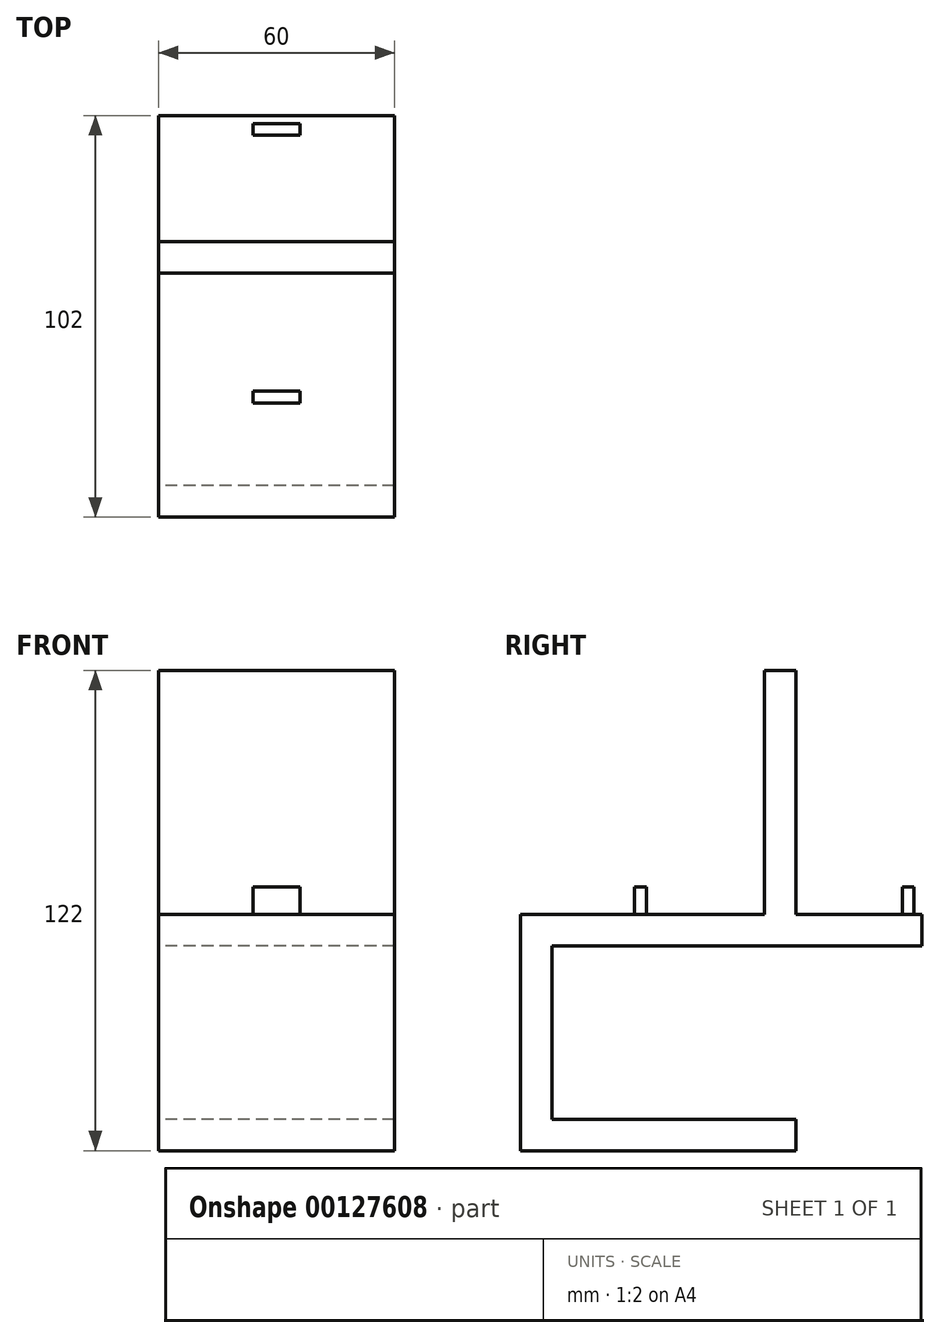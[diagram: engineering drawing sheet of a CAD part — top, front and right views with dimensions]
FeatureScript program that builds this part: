
annotation { "Feature Type Name" : "Feature", "Feature Type Description" : "" }
export const myFeature = defineFeature(function(context is Context, id is Id, definition is map)
    precondition{}
    {
        {
            var Q0;
            Q0=qCreatedBy(makeId("Right.planeOp"),FACE);
            var sketch = newSketch(context, id + "F0", { "sketchPlane" : qUnion([Q0])});
            skLineSegment(sketch, "E0.bottom", {"start": v(129.92, 70) * mm, "end": v(121.92, 70) * mm});
            skLineSegment(sketch, "E0.top", {"start": v(129.92, 0) * mm, "end": v(121.92, 0) * mm});
            skLineSegment(sketch, "E0.left", {"start": v(129.92, 70) * mm, "end": v(129.92, 0) * mm});
            skLineSegment(sketch, "E0.right", {"start": v(121.92, 70) * mm, "end": v(121.92, 0) * mm});
            skLineSegment(sketch, "E1.bottom", {"start": v(121.92, 8) * mm, "end": v(59.92, 8) * mm});
            skLineSegment(sketch, "E1.top", {"start": v(121.92, 0) * mm, "end": v(59.92, 0) * mm});
            skLineSegment(sketch, "E1.left", {"start": v(121.92, 8) * mm, "end": v(121.92, 0) * mm});
            skLineSegment(sketch, "E1.right", {"start": v(59.92, 8) * mm, "end": v(59.92, 0) * mm});
            skLineSegment(sketch, "E2.bottom", {"start": v(59.92, 0) * mm, "end": v(67.92, 0) * mm});
            skLineSegment(sketch, "E2.top", {"start": v(59.92, -52) * mm, "end": v(67.92, -52) * mm});
            skLineSegment(sketch, "E2.left", {"start": v(59.92, 0) * mm, "end": v(59.92, -52) * mm});
            skLineSegment(sketch, "E2.right", {"start": v(67.92, 0) * mm, "end": v(67.92, -52) * mm});
            skLineSegment(sketch, "E3.bottom", {"start": v(67.92, -52) * mm, "end": v(129.92, -52) * mm});
            skLineSegment(sketch, "E3.top", {"start": v(67.92, -44) * mm, "end": v(129.92, -44) * mm});
            skLineSegment(sketch, "E3.left", {"start": v(67.92, -52) * mm, "end": v(67.92, -44) * mm});
            skLineSegment(sketch, "E3.right", {"start": v(129.92, -52) * mm, "end": v(129.92, -44) * mm});
            skSolve(sketch);
        }
        {
            var Q0;
            Q0 = qSketchRegion(id + "F0", true);
            extrude(context, id + "F1", {"entities" : qUnion([Q0]), "depth" : 60 * mm});
        }
        {
            var Q0;
            Q0=qCreatedBy(makeId("Top.planeOp"),FACE);
            var sketch = newSketch(context, id + "F2", { "sketchPlane" : qUnion([Q0])});
            skLineSegment(sketch, "E4.0.0", {"start": v(0, 121.92) * mm, "end": v(0, 59.92) * mm});
            skLineSegment(sketch, "E4.0.1", {"start": v(0, 59.92) * mm, "end": v(60, 59.92) * mm});
            skLineSegment(sketch, "E4.0.2", {"start": v(60, 59.92) * mm, "end": v(60, 121.92) * mm});
            skLineSegment(sketch, "E4.0.3", {"start": v(60, 121.92) * mm, "end": v(0, 121.92) * mm});
            skLineSegment(sketch, "E5.bottom", {"start": v(24, 91.92) * mm, "end": v(36, 91.92) * mm});
            skLineSegment(sketch, "E5.top", {"start": v(24, 88.92) * mm, "end": v(36, 88.92) * mm});
            skLineSegment(sketch, "E5.left", {"start": v(24, 91.92) * mm, "end": v(24, 88.92) * mm});
            skLineSegment(sketch, "E5.right", {"start": v(36, 91.92) * mm, "end": v(36, 88.92) * mm});
            skPoint(sketch, "E5.middle", {"position": v(30, 90.42) * mm});
            skSolve(sketch);
        }
        {
            var Q0;
            Q0=makeQuery(id+"F2.imprint","IMPRINT",FACE,{"disambiguationData":[TD([[makeQuery(id+"F2.imprint","IMPRINT",EDGE,{"derivedFrom":sQuery(id+"F2.wireOp",EDGE,"E5.bottom")}),-1.0]])]});
            extrude(context, id + "F3", {"entities" : qUnion([Q0]), "operationType" : NewBodyOperationType.ADD, "depth" : 15 * mm});
        }
        {
            var Q0;
            Q0=qCreatedBy(makeId("Right.planeOp"),FACE);
            var sketch = newSketch(context, id + "F4", { "sketchPlane" : qUnion([Q0])});
            skLineSegment(sketch, "E6.0.0", {"start": v(129.92, 70) * mm, "end": v(129.92, 0) * mm});
            skLineSegment(sketch, "E6.0.1", {"start": v(129.92, 0) * mm, "end": v(67.92, 0) * mm});
            skLineSegment(sketch, "E6.0.2", {"start": v(67.92, 0) * mm, "end": v(67.92, -44) * mm});
            skLineSegment(sketch, "E6.0.3", {"start": v(67.92, -44) * mm, "end": v(129.92, -44) * mm});
            skLineSegment(sketch, "E6.0.4", {"start": v(129.92, -44) * mm, "end": v(129.92, -52) * mm});
            skLineSegment(sketch, "E6.0.5", {"start": v(129.92, -52) * mm, "end": v(59.92, -52) * mm});
            skLineSegment(sketch, "E6.0.6", {"start": v(59.92, -52) * mm, "end": v(59.92, 8) * mm});
            skLineSegment(sketch, "E6.0.7", {"start": v(59.92, 8) * mm, "end": v(121.92, 8) * mm});
            skLineSegment(sketch, "E6.0.8", {"start": v(121.92, 8) * mm, "end": v(121.92, 70) * mm});
            skLineSegment(sketch, "E6.0.9", {"start": v(121.92, 70) * mm, "end": v(129.92, 70) * mm});
            skLineSegment(sketch, "E7.bottom", {"start": v(121.92, 8) * mm, "end": v(161.92, 8) * mm});
            skLineSegment(sketch, "E7.top", {"start": v(121.92, 0) * mm, "end": v(161.92, 0) * mm});
            skLineSegment(sketch, "E7.left", {"start": v(121.92, 8) * mm, "end": v(121.92, 0) * mm});
            skLineSegment(sketch, "E7.right", {"start": v(161.92, 8) * mm, "end": v(161.92, 0) * mm});
            skSolve(sketch);
        }
        {
            var Q0;
            Q0 = qSketchRegion(id + "F4", true);
            extrude(context, id + "F5", {"entities" : qUnion([Q0]), "operationType" : NewBodyOperationType.ADD, "depth" : 60 * mm});
        }
        {
            var Q0;
            Q0=qCreatedBy(makeId("Top.planeOp"),FACE);
            var sketch = newSketch(context, id + "F6", { "sketchPlane" : qUnion([Q0])});
            skLineSegment(sketch, "E8.0.0", {"start": v(0, 161.92) * mm, "end": v(0, 129.92) * mm});
            skLineSegment(sketch, "E8.0.1", {"start": v(0, 129.92) * mm, "end": v(60, 129.92) * mm});
            skLineSegment(sketch, "E8.0.2", {"start": v(60, 129.92) * mm, "end": v(60, 161.92) * mm});
            skLineSegment(sketch, "E8.0.3", {"start": v(60, 161.92) * mm, "end": v(0, 161.92) * mm});
            skLineSegment(sketch, "E9.0.0", {"start": v(36, 91.92) * mm, "end": v(24, 91.92) * mm});
            skLineSegment(sketch, "E9.0.1", {"start": v(24, 91.92) * mm, "end": v(24, 88.92) * mm});
            skLineSegment(sketch, "E9.0.2", {"start": v(24, 88.92) * mm, "end": v(36, 88.92) * mm});
            skLineSegment(sketch, "E9.0.3", {"start": v(36, 88.92) * mm, "end": v(36, 91.92) * mm});
            skLineSegment(sketch, "E10.bottom", {"start": v(24, 159.92) * mm, "end": v(36, 159.92) * mm});
            skLineSegment(sketch, "E10.top", {"start": v(24, 156.92) * mm, "end": v(36, 156.92) * mm});
            skLineSegment(sketch, "E10.left", {"start": v(24, 159.92) * mm, "end": v(24, 156.92) * mm});
            skLineSegment(sketch, "E10.right", {"start": v(36, 159.92) * mm, "end": v(36, 156.92) * mm});
            skSolve(sketch);
        }
        {
            var Q0;
            Q0=makeQuery(id+"F6.imprint","IMPRINT",FACE,{"disambiguationData":[TD([[makeQuery(id+"F6.imprint","IMPRINT",EDGE,{"derivedFrom":sQuery(id+"F6.wireOp",EDGE,"E10.bottom")}),-1.0]])]});
            extrude(context, id + "F7", {"entities" : qUnion([Q0]), "operationType" : NewBodyOperationType.ADD, "depth" : 15 * mm});
        }
    });
